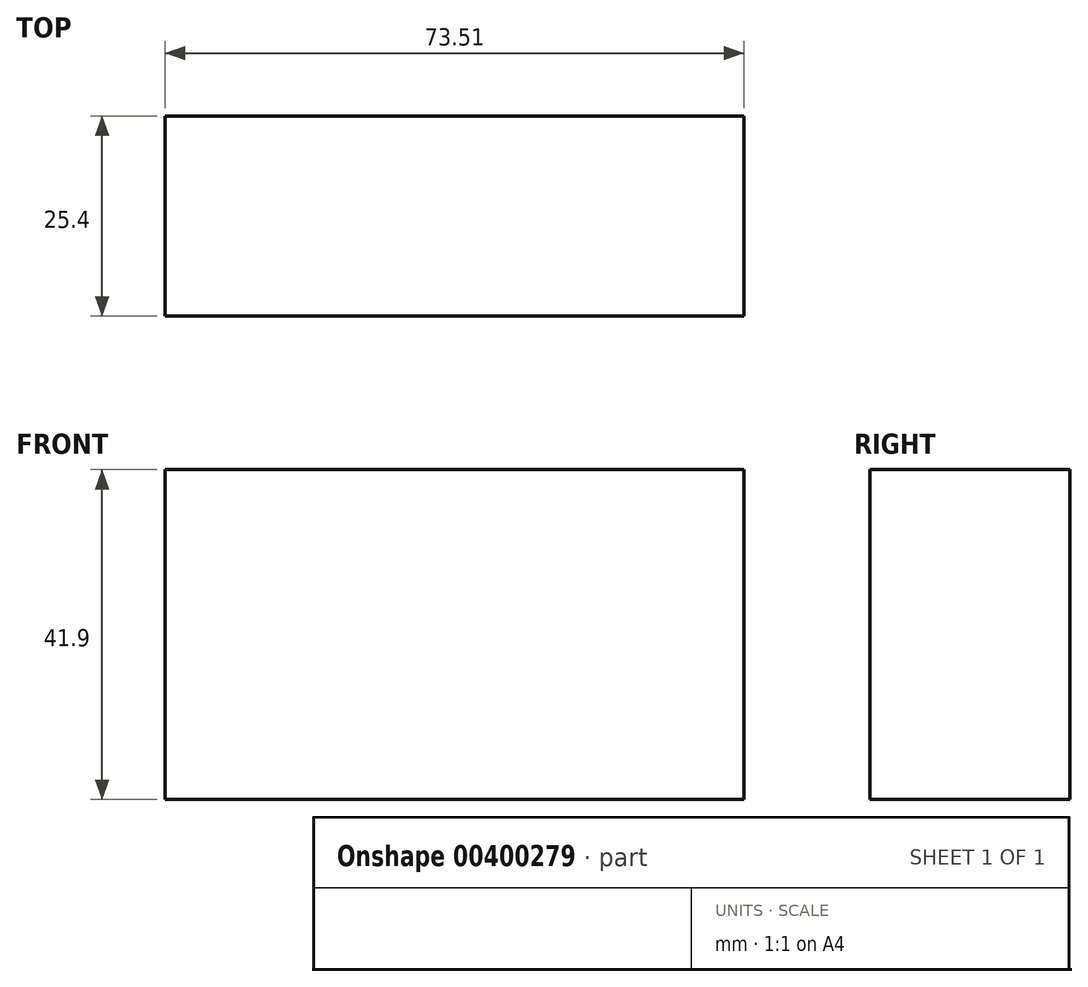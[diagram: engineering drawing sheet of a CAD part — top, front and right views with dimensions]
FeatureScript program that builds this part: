
annotation { "Feature Type Name" : "Feature", "Feature Type Description" : "" }
export const myFeature = defineFeature(function(context is Context, id is Id, definition is map)
    precondition{}
    {
        {
            var Q0;
            Q0=qCreatedBy(makeId("Front.planeOp"),FACE);
            var sketch = newSketch(context, id + "F0", { "sketchPlane" : qUnion([Q0])});
            skLineSegment(sketch, "E0.bottom", {"start": v(-37.63, 21.83) * mm, "end": v(35.88, 21.83) * mm});
            skLineSegment(sketch, "E0.top", {"start": v(-37.63, -20.07) * mm, "end": v(35.88, -20.07) * mm});
            skLineSegment(sketch, "E0.left", {"start": v(-37.63, 21.83) * mm, "end": v(-37.63, -20.07) * mm});
            skLineSegment(sketch, "E0.right", {"start": v(35.88, 21.83) * mm, "end": v(35.88, -20.07) * mm});
            skSolve(sketch);
        }
        {
            var Q0;
            Q0=qSketchRegion(id+"F0",true);
            extrude(context, id + "F1", {"entities" : qUnion([Q0]), "depth" : 25.4 * mm});
        }
    });
